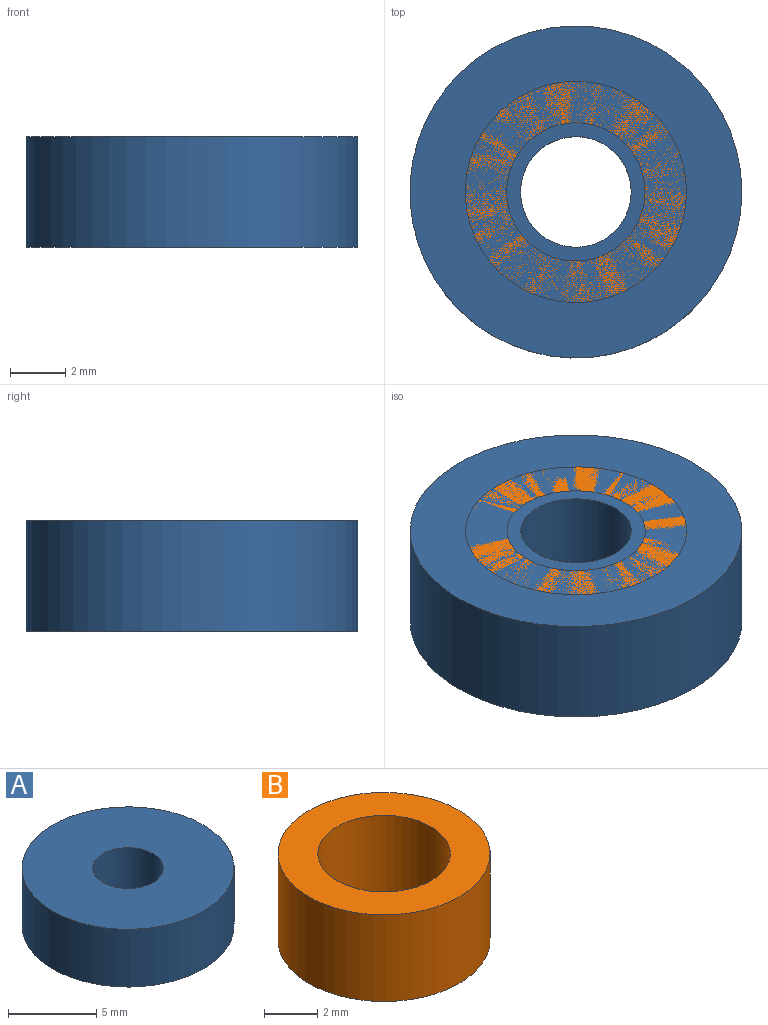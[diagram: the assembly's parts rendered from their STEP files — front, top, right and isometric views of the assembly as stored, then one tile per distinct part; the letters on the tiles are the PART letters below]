
ASSEMBLY  parts=2 mates=1
PART A: 4 faces, bbox 12x12x4 mm
  f0: cylinder r=2mm len=4mm, axis (0,0,-1), area 50.3mm2, adj f2,f3
  f1: cylinder r=6mm len=12mm, axis (0,0,-1), area 150.8mm2, adj f2,f3
  f2: plane 12x12mm, normal (0,0,1), area 100.5mm2, adj f0,f1
  f3: plane 12x12mm, normal (0,0,-1), area 100.5mm2, adj f0,f1
PART B: 4 faces, bbox 8x8x4 mm
  f0: cylinder r=2.5mm len=5mm, axis (0,0,-1), area 62.8mm2, adj f2,f3
  f1: cylinder r=4mm len=8mm, axis (0,0,-1), area 100.5mm2, adj f2,f3
  f2: plane 8x8mm, normal (0,0,1), area 30.6mm2, adj f0,f1
  f3: plane 8x8mm, normal (0,0,-1), area 30.6mm2, adj f0,f1
PLACE A t=(-4.94,0.46,2.98)mm
PLACE B t=(-4.94,0.46,2.98)mm
MATE revolute B.f1 <-> A.f1  axis (0,0,-1) through (-4.94,0.46,6.98)mm
